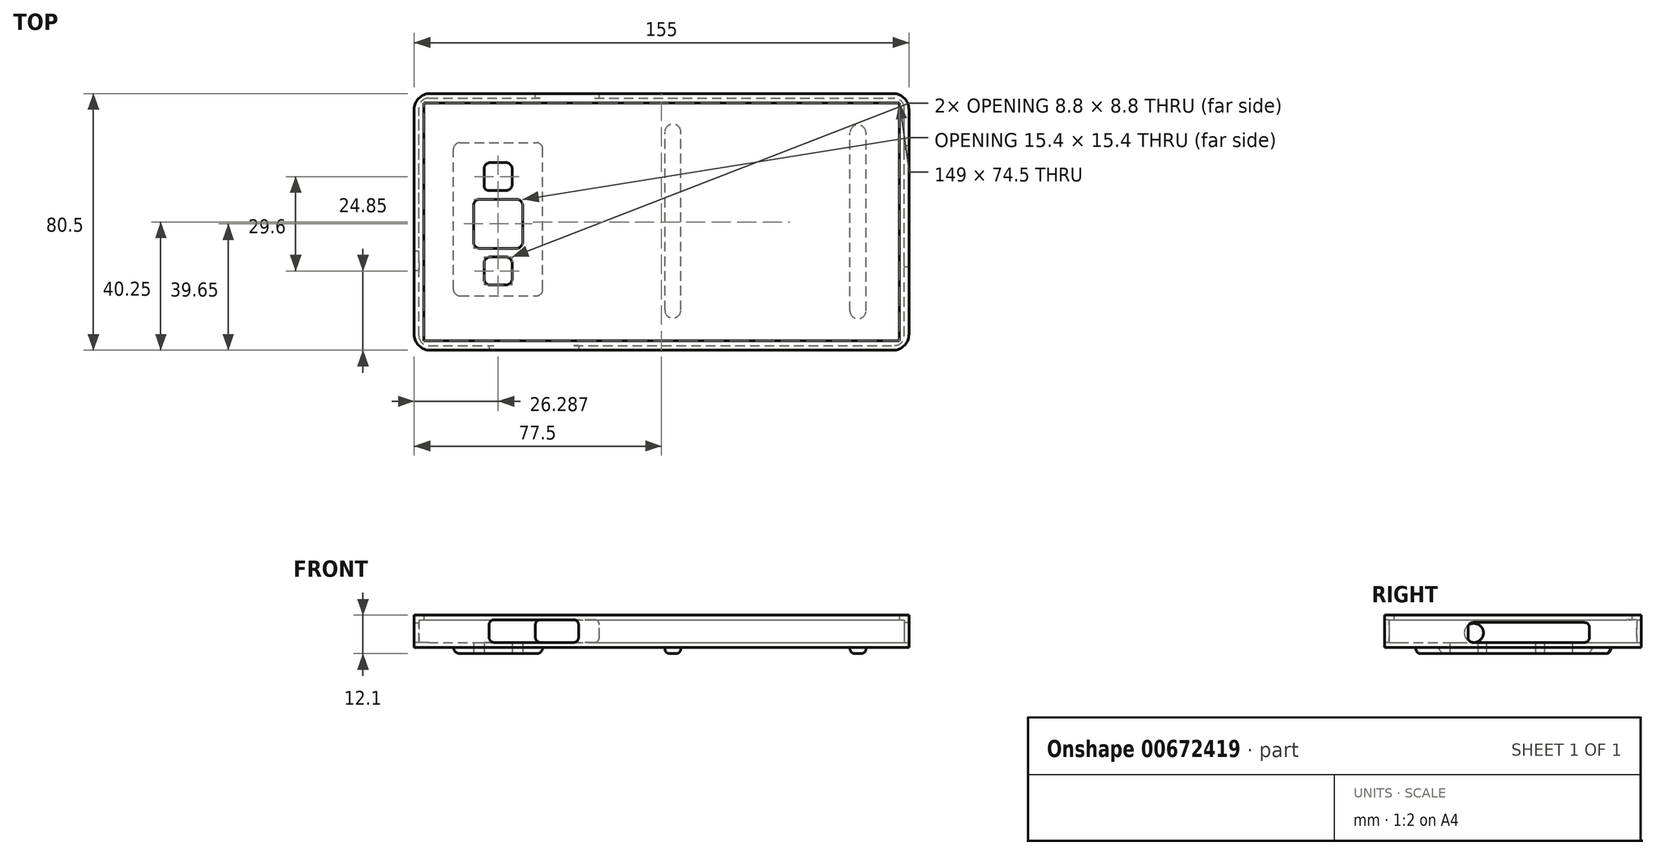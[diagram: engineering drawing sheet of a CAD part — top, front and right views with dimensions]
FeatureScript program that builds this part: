
annotation { "Feature Type Name" : "Feature", "Feature Type Description" : "" }
export const myFeature = defineFeature(function(context is Context, id is Id, definition is map)
    precondition{}
    {
        {
            var Q0;
            Q0=qCreatedBy(makeId("Top.planeOp"),FACE);
            var sketch = newSketch(context, id + "F0", { "sketchPlane" : qUnion([Q0])});
            skLineSegment(sketch, "E0.bottom", {"start": v(0, 0) * mm, "end": v(155, 0) * mm});
            skLineSegment(sketch, "E0.top", {"start": v(0, 80.5) * mm, "end": v(155, 80.5) * mm});
            skLineSegment(sketch, "E0.left", {"start": v(0, 0) * mm, "end": v(0, 80.5) * mm});
            skLineSegment(sketch, "E0.right", {"start": v(155, 0) * mm, "end": v(155, 80.5) * mm});
            skSolve(sketch);
        }
        {
            var Q0;
            Q0=qSketchRegion(id+"F0",true);
            extrude(context, id + "F1", {"entities" : qUnion([Q0]), "depth" : 8.6 * mm, "offsetDistance" : 25 * mm});
        }
        {
            var Q0;
            Q0=makeQuery(id+"F1.opExtrude","CAP_FACE",FACE,{"disambiguationData":[OSD([sQuery(id+"F0.wireOp",EDGE,"E0.bottom"),sQuery(id+"F0.wireOp",EDGE,"E0.top"),sQuery(id+"F0.wireOp",EDGE,"E0.left"),sQuery(id+"F0.wireOp",EDGE,"E0.right")])],"isStart":false});
            shell(context, id + "F2", {"entities" : qUnion([Q0]), "thickness" : 1.5 * mm});
        }
        {
            var Q0;
            Q0=makeQuery(id+"F1.opExtrude","CAP_FACE",FACE,{"disambiguationData":[OSD([sQuery(id+"F0.wireOp",EDGE,"E0.bottom"),sQuery(id+"F0.wireOp",EDGE,"E0.top"),sQuery(id+"F0.wireOp",EDGE,"E0.left"),sQuery(id+"F0.wireOp",EDGE,"E0.right")])],"isStart":false});
            var sketch = newSketch(context, id + "F3", { "sketchPlane" : qUnion([Q0])});
            skLineSegment(sketch, "E1.0", {"start": v(3, 77.5) * mm, "end": v(152, 77.5) * mm});
            skLineSegment(sketch, "E1.1", {"start": v(3, 3) * mm, "end": v(3, 77.5) * mm});
            skLineSegment(sketch, "E1.2", {"start": v(3, 3) * mm, "end": v(152, 3) * mm});
            skLineSegment(sketch, "E1.3", {"start": v(152, 3) * mm, "end": v(152, 77.5) * mm});
            skSolve(sketch);
        }
        {
            var Q0;
            Q0=makeQuery(id+"F3.imprint","IMPRINT",FACE,{"disambiguationData":[TD([[makeQuery(id+"F3.imprint","IMPRINT",EDGE,{"derivedFrom":sQuery(id+"F3.wireOp",EDGE,"E1.0")}),1.0]])]});
            var Q1;
            {var subQ6=sQuery(id+"F0.wireOp",EDGE,"E0.bottom");var subQ7=makeQuery(id+"F1.opExtrude","CAP_EDGE",EDGE,{"disambiguationData":[OSD([subQ6])],"isStart":false});Q1=makeQuery(id+"F3.imprint","IMPRINT",FACE,{"disambiguationData":[TD([[makeQuery(id+"F3.imprint","IMPRINT",EDGE,{"derivedFrom":subQ7}),1.0]])]});}
            extrude(context, id + "F4", {"entities" : qUnion([Q0, Q1]), "operationType" : NewBodyOperationType.ADD, "depth" : 1.5 * mm, "offsetDistance" : 25 * mm});
        }
        {
            var Q0;
            {var subQ0=sQuery(id+"F0.wireOp",EDGE,"E0.bottom");Q0=makeQuery(id+"F4.boolean.opBoolean","MERGE",FACE,{"derivedFrom":[makeQuery(id+"F1.opExtrude","SWEPT_FACE",FACE,{"disambiguationData":[OSD([subQ0])]}),makeQuery(id+"F4.opExtrude","SWEPT_FACE",FACE,{"disambiguationData":[OSD([subQ0])]})]});}
            var sketch = newSketch(context, id + "F5", { "sketchPlane" : qUnion([Q0])});
            skLineSegment(sketch, "E2.bottom", {"start": v(23.5, 8.6) * mm, "end": v(51.5, 8.6) * mm});
            skLineSegment(sketch, "E2.top", {"start": v(23.5, 1.5) * mm, "end": v(51.5, 1.5) * mm});
            skLineSegment(sketch, "E2.left", {"start": v(23.5, 8.6) * mm, "end": v(23.5, 1.5) * mm});
            skLineSegment(sketch, "E2.right", {"start": v(51.5, 8.6) * mm, "end": v(51.5, 1.5) * mm});
            skSolve(sketch);
        }
        {
            var Q0;
            Q0=makeQuery(id+"F5.imprint","IMPRINT",FACE,{"disambiguationData":[TD([[makeQuery(id+"F5.imprint","IMPRINT",EDGE,{"derivedFrom":sQuery(id+"F5.wireOp",EDGE,"E2.bottom")}),-1.0]])]});
            extrude(context, id + "F6", {"entities" : qUnion([Q0]), "operationType" : NewBodyOperationType.REMOVE, "endBound" : BoundingType.UP_TO_NEXT, "oppositeDirection" : true, "depth" : 25 * mm, "offsetDistance" : 25 * mm});
        }
        {
            var Q0;
            {var subQ0=sQuery(id+"F0.wireOp",EDGE,"E0.top");Q0=makeQuery(id+"F4.boolean.opBoolean","MERGE",FACE,{"derivedFrom":[makeQuery(id+"F1.opExtrude","SWEPT_FACE",FACE,{"disambiguationData":[OSD([subQ0])]}),makeQuery(id+"F4.opExtrude","SWEPT_FACE",FACE,{"disambiguationData":[OSD([subQ0])]})]});}
            var sketch = newSketch(context, id + "F7", { "sketchPlane" : qUnion([Q0])});
            skLineSegment(sketch, "E3.bottom", {"start": v(-58, 8.6) * mm, "end": v(-38, 8.6) * mm});
            skLineSegment(sketch, "E3.top", {"start": v(-58, 1.5) * mm, "end": v(-38, 1.5) * mm});
            skLineSegment(sketch, "E3.left", {"start": v(-58, 8.6) * mm, "end": v(-58, 1.5) * mm});
            skLineSegment(sketch, "E3.right", {"start": v(-38, 8.6) * mm, "end": v(-38, 1.5) * mm});
            skSolve(sketch);
        }
        {
            var Q0;
            Q0=makeQuery(id+"F7.imprint","IMPRINT",FACE,{"disambiguationData":[TD([[makeQuery(id+"F7.imprint","IMPRINT",EDGE,{"derivedFrom":sQuery(id+"F7.wireOp",EDGE,"E3.bottom")}),-1.0]])]});
            extrude(context, id + "F8", {"entities" : qUnion([Q0]), "operationType" : NewBodyOperationType.REMOVE, "endBound" : BoundingType.UP_TO_NEXT, "oppositeDirection" : true, "depth" : 25 * mm, "offsetDistance" : 25 * mm});
        }
        {
            var Q0;
            {var subQ0=sQuery(id+"F0.wireOp",EDGE,"E0.left");Q0=makeQuery(id+"F4.boolean.opBoolean","MERGE",FACE,{"derivedFrom":[makeQuery(id+"F1.opExtrude","SWEPT_FACE",FACE,{"disambiguationData":[OSD([subQ0])]}),makeQuery(id+"F4.opExtrude","SWEPT_FACE",FACE,{"disambiguationData":[OSD([subQ0])]})]});}
            var sketch = newSketch(context, id + "F9", { "sketchPlane" : qUnion([Q0])});
            skCircle(sketch, "E4", {"center": v(-28, 4.5) * mm, "radius": 3 * mm});
            skSolve(sketch);
        }
        {
            var Q0;
            Q0=makeQuery(id+"F9.imprint","IMPRINT",FACE,{"disambiguationData":[TD([[makeQuery(id+"F9.imprint","IMPRINT",EDGE,{"derivedFrom":sQuery(id+"F9.wireOp",EDGE,"E4")}),1.0]])]});
            extrude(context, id + "F10", {"entities" : qUnion([Q0]), "operationType" : NewBodyOperationType.REMOVE, "endBound" : BoundingType.UP_TO_NEXT, "oppositeDirection" : true, "depth" : 25 * mm, "offsetDistance" : 25 * mm});
        }
        {
            var Q0;
            {var subQ0=sQuery(id+"F0.wireOp",EDGE,"E0.right");Q0=makeQuery(id+"F4.boolean.opBoolean","MERGE",FACE,{"derivedFrom":[makeQuery(id+"F1.opExtrude","SWEPT_FACE",FACE,{"disambiguationData":[OSD([subQ0])]}),makeQuery(id+"F4.opExtrude","SWEPT_FACE",FACE,{"disambiguationData":[OSD([subQ0])]})]});}
            var sketch = newSketch(context, id + "F11", { "sketchPlane" : qUnion([Q0])});
            skLineSegment(sketch, "E5.bottom", {"start": v(26.2, 7.75) * mm, "end": v(64.2, 7.75) * mm});
            skLineSegment(sketch, "E5.top", {"start": v(26.2, 1.5) * mm, "end": v(64.2, 1.5) * mm});
            skLineSegment(sketch, "E5.left", {"start": v(26.2, 7.75) * mm, "end": v(26.2, 1.5) * mm});
            skLineSegment(sketch, "E5.right", {"start": v(64.2, 7.75) * mm, "end": v(64.2, 1.5) * mm});
            skSolve(sketch);
        }
        {
            var Q0;
            Q0=makeQuery(id+"F11.imprint","IMPRINT",FACE,{"disambiguationData":[TD([[makeQuery(id+"F11.imprint","IMPRINT",EDGE,{"derivedFrom":sQuery(id+"F11.wireOp",EDGE,"E5.bottom")}),-1.0]])]});
            extrude(context, id + "F12", {"entities" : qUnion([Q0]), "operationType" : NewBodyOperationType.REMOVE, "endBound" : BoundingType.UP_TO_NEXT, "oppositeDirection" : true, "depth" : 25 * mm, "offsetDistance" : 25 * mm});
        }
        {
            var Q0;
            Q0=makeQuery(id+"F1.opExtrude","CAP_FACE",FACE,{"disambiguationData":[OSD([sQuery(id+"F0.wireOp",EDGE,"E0.bottom"),sQuery(id+"F0.wireOp",EDGE,"E0.top"),sQuery(id+"F0.wireOp",EDGE,"E0.left"),sQuery(id+"F0.wireOp",EDGE,"E0.right")])],"isStart":true});
            var sketch = newSketch(context, id + "F13", { "sketchPlane" : qUnion([Q0])});
            skLineSegment(sketch, "E6.bottom", {"start": v(21.89, -20.45) * mm, "end": v(30.69, -20.45) * mm});
            skLineSegment(sketch, "E6.top", {"start": v(21.89, -29.25) * mm, "end": v(30.69, -29.25) * mm});
            skLineSegment(sketch, "E6.left", {"start": v(21.89, -20.45) * mm, "end": v(21.89, -29.25) * mm});
            skLineSegment(sketch, "E6.right", {"start": v(30.69, -20.45) * mm, "end": v(30.69, -29.25) * mm});
            skLineSegment(sketch, "E7.bottom", {"start": v(18.59, -31.95) * mm, "end": v(33.99, -31.95) * mm});
            skLineSegment(sketch, "E7.top", {"start": v(18.59, -47.35) * mm, "end": v(33.99, -47.35) * mm});
            skLineSegment(sketch, "E7.left", {"start": v(18.59, -31.95) * mm, "end": v(18.59, -47.35) * mm});
            skLineSegment(sketch, "E7.right", {"start": v(33.99, -31.95) * mm, "end": v(33.99, -47.35) * mm});
            skLineSegment(sketch, "E8.bottom", {"start": v(21.89, -50.05) * mm, "end": v(30.69, -50.05) * mm});
            skLineSegment(sketch, "E8.top", {"start": v(21.89, -58.85) * mm, "end": v(30.69, -58.85) * mm});
            skLineSegment(sketch, "E8.left", {"start": v(21.89, -50.05) * mm, "end": v(21.89, -58.85) * mm});
            skLineSegment(sketch, "E8.right", {"start": v(30.69, -50.05) * mm, "end": v(30.69, -58.85) * mm});
            skLineSegment(sketch, "E9", {"start": v(12.52, -39.65) * mm, "end": v(41, -39.65) * mm});
            skPoint(sketch, "E9.startSnap0", {"position": v(18.59, -39.65) * mm});
            skLineSegment(sketch, "E10", {"start": v(16.62, -24.85) * mm, "end": v(34.64, -24.85) * mm});
            skPoint(sketch, "E10.startSnap0", {"position": v(21.89, -24.85) * mm});
            skLineSegment(sketch, "E11", {"start": v(16.41, -54.45) * mm, "end": v(34.85, -54.45) * mm});
            skPoint(sketch, "E11.startSnap0", {"position": v(21.89, -54.45) * mm});
            skSolve(sketch);
        }
        {
            var Q0;
            {var subQ0=sQuery(id+"F13.wireOp",EDGE,"E6.top");Q0=makeQuery(id+"F13.imprint","IMPRINT",FACE,{"disambiguationData":[TD([[makeQuery(id+"F13.imprint","IMPRINT",EDGE,{"derivedFrom":subQ0}),1.0]])]});}
            var Q1;
            {var subQ0=sQuery(id+"F13.wireOp",EDGE,"E6.bottom");Q1=makeQuery(id+"F13.imprint","IMPRINT",FACE,{"disambiguationData":[TD([[makeQuery(id+"F13.imprint","IMPRINT",EDGE,{"derivedFrom":subQ0}),-1.0]])]});}
            var Q2;
            {var subQ0=sQuery(id+"F13.wireOp",EDGE,"E7.bottom");Q2=makeQuery(id+"F13.imprint","IMPRINT",FACE,{"disambiguationData":[TD([[makeQuery(id+"F13.imprint","IMPRINT",EDGE,{"derivedFrom":subQ0}),-1.0]])]});}
            var Q3;
            {var subQ0=sQuery(id+"F13.wireOp",EDGE,"E7.top");Q3=makeQuery(id+"F13.imprint","IMPRINT",FACE,{"disambiguationData":[TD([[makeQuery(id+"F13.imprint","IMPRINT",EDGE,{"derivedFrom":subQ0}),1.0]])]});}
            var Q4;
            {var subQ0=sQuery(id+"F13.wireOp",EDGE,"E8.bottom");Q4=makeQuery(id+"F13.imprint","IMPRINT",FACE,{"disambiguationData":[TD([[makeQuery(id+"F13.imprint","IMPRINT",EDGE,{"derivedFrom":subQ0}),-1.0]])]});}
            var Q5;
            {var subQ0=sQuery(id+"F13.wireOp",EDGE,"E8.top");Q5=makeQuery(id+"F13.imprint","IMPRINT",FACE,{"disambiguationData":[TD([[makeQuery(id+"F13.imprint","IMPRINT",EDGE,{"derivedFrom":subQ0}),1.0]])]});}
            extrude(context, id + "F14", {"entities" : qUnion([Q0, Q1, Q2, Q3, Q4, Q5]), "operationType" : NewBodyOperationType.REMOVE, "endBound" : BoundingType.UP_TO_NEXT, "oppositeDirection" : true, "depth" : 25 * mm, "offsetDistance" : 25 * mm});
        }
        {
            var Q0;
            Q0=makeQuery(id+"F6.boolean.opBoolean","COPY",EDGE,{"derivedFrom":makeQuery(id+"F6.opExtrude","SWEPT_EDGE",EDGE,{"disambiguationData":[OSD([sQuery(id+"F5.wireOp",EDGE,"E2.bottom"),sQuery(id+"F5.wireOp",EDGE,"E2.left")])]})});
            var Q1;
            Q1=makeQuery(id+"F6.boolean.opBoolean","COPY",EDGE,{"derivedFrom":makeQuery(id+"F6.opExtrude","SWEPT_EDGE",EDGE,{"disambiguationData":[OSD([sQuery(id+"F5.wireOp",EDGE,"E2.bottom"),sQuery(id+"F5.wireOp",EDGE,"E2.right")])]})});
            var Q2;
            Q2=makeQuery(id+"F6.boolean.opBoolean","COPY",EDGE,{"derivedFrom":makeQuery(id+"F6.opExtrude","SWEPT_EDGE",EDGE,{"disambiguationData":[OSD([sQuery(id+"F5.wireOp",EDGE,"E2.top"),sQuery(id+"F5.wireOp",EDGE,"E2.right")])]})});
            var Q3;
            Q3=makeQuery(id+"F6.boolean.opBoolean","COPY",EDGE,{"derivedFrom":makeQuery(id+"F6.opExtrude","SWEPT_EDGE",EDGE,{"disambiguationData":[OSD([sQuery(id+"F5.wireOp",EDGE,"E2.top"),sQuery(id+"F5.wireOp",EDGE,"E2.left")])]})});
            var Q4;
            Q4=makeQuery(id+"F12.boolean.opBoolean","COPY",EDGE,{"derivedFrom":makeQuery(id+"F12.opExtrude","SWEPT_EDGE",EDGE,{"disambiguationData":[OSD([sQuery(id+"F11.wireOp",EDGE,"E5.bottom"),sQuery(id+"F11.wireOp",EDGE,"E5.left")])]})});
            var Q5;
            Q5=makeQuery(id+"F12.boolean.opBoolean","COPY",EDGE,{"derivedFrom":makeQuery(id+"F12.opExtrude","SWEPT_EDGE",EDGE,{"disambiguationData":[OSD([sQuery(id+"F11.wireOp",EDGE,"E5.top"),sQuery(id+"F11.wireOp",EDGE,"E5.left")])]})});
            var Q6;
            Q6=makeQuery(id+"F12.boolean.opBoolean","COPY",EDGE,{"derivedFrom":makeQuery(id+"F12.opExtrude","SWEPT_EDGE",EDGE,{"disambiguationData":[OSD([sQuery(id+"F11.wireOp",EDGE,"E5.bottom"),sQuery(id+"F11.wireOp",EDGE,"E5.right")])]})});
            var Q7;
            Q7=makeQuery(id+"F12.boolean.opBoolean","COPY",EDGE,{"derivedFrom":makeQuery(id+"F12.opExtrude","SWEPT_EDGE",EDGE,{"disambiguationData":[OSD([sQuery(id+"F11.wireOp",EDGE,"E5.top"),sQuery(id+"F11.wireOp",EDGE,"E5.right")])]})});
            var Q8;
            Q8=makeQuery(id+"F8.boolean.opBoolean","COPY",EDGE,{"derivedFrom":makeQuery(id+"F8.opExtrude","SWEPT_EDGE",EDGE,{"disambiguationData":[OSD([sQuery(id+"F7.wireOp",EDGE,"E3.bottom"),sQuery(id+"F7.wireOp",EDGE,"E3.left")])]})});
            var Q9;
            Q9=makeQuery(id+"F8.boolean.opBoolean","COPY",EDGE,{"derivedFrom":makeQuery(id+"F8.opExtrude","SWEPT_EDGE",EDGE,{"disambiguationData":[OSD([sQuery(id+"F7.wireOp",EDGE,"E3.top"),sQuery(id+"F7.wireOp",EDGE,"E3.left")])]})});
            var Q10;
            Q10=makeQuery(id+"F8.boolean.opBoolean","COPY",EDGE,{"derivedFrom":makeQuery(id+"F8.opExtrude","SWEPT_EDGE",EDGE,{"disambiguationData":[OSD([sQuery(id+"F7.wireOp",EDGE,"E3.bottom"),sQuery(id+"F7.wireOp",EDGE,"E3.right")])]})});
            var Q11;
            Q11=makeQuery(id+"F8.boolean.opBoolean","COPY",EDGE,{"derivedFrom":makeQuery(id+"F8.opExtrude","SWEPT_EDGE",EDGE,{"disambiguationData":[OSD([sQuery(id+"F7.wireOp",EDGE,"E3.top"),sQuery(id+"F7.wireOp",EDGE,"E3.right")])]})});
            var Q12;
            Q12=makeQuery(id+"F14.boolean.opBoolean","COPY",EDGE,{"derivedFrom":makeQuery(id+"F14.opExtrude","SWEPT_EDGE",EDGE,{"disambiguationData":[OSD([sQuery(id+"F13.wireOp",EDGE,"E8.bottom"),sQuery(id+"F13.wireOp",EDGE,"E8.left")])]})});
            fillet(context, id + "F15", {"entities" : qUnion([Q0, Q1, Q2, Q3, Q4, Q5, Q6, Q7, Q8, Q9, Q10, Q11, Q12]), "radius" : 1.5 * mm, "tangentPropagation" : true, "allowEdgeOverflow" : false});
        }
        {
            var Q0;
            Q0=makeQuery(id+"F14.boolean.opBoolean","COPY",EDGE,{"derivedFrom":makeQuery(id+"F14.opExtrude","SWEPT_EDGE",EDGE,{"disambiguationData":[OSD([sQuery(id+"F13.wireOp",EDGE,"E6.top"),sQuery(id+"F13.wireOp",EDGE,"E6.left")])]})});
            var Q1;
            Q1=makeQuery(id+"F14.boolean.opBoolean","COPY",EDGE,{"derivedFrom":makeQuery(id+"F14.opExtrude","SWEPT_EDGE",EDGE,{"disambiguationData":[OSD([sQuery(id+"F13.wireOp",EDGE,"E7.top"),sQuery(id+"F13.wireOp",EDGE,"E7.left")])]})});
            var Q2;
            Q2=makeQuery(id+"F14.boolean.opBoolean","COPY",EDGE,{"derivedFrom":makeQuery(id+"F14.opExtrude","SWEPT_EDGE",EDGE,{"disambiguationData":[OSD([sQuery(id+"F13.wireOp",EDGE,"E8.top"),sQuery(id+"F13.wireOp",EDGE,"E8.left")])]})});
            var Q3;
            Q3=makeQuery(id+"F14.boolean.opBoolean","COPY",EDGE,{"derivedFrom":makeQuery(id+"F14.opExtrude","SWEPT_EDGE",EDGE,{"disambiguationData":[OSD([sQuery(id+"F13.wireOp",EDGE,"E6.bottom"),sQuery(id+"F13.wireOp",EDGE,"E6.left")])]})});
            var Q4;
            Q4=makeQuery(id+"F14.boolean.opBoolean","COPY",EDGE,{"derivedFrom":makeQuery(id+"F14.opExtrude","SWEPT_EDGE",EDGE,{"disambiguationData":[OSD([sQuery(id+"F13.wireOp",EDGE,"E7.bottom"),sQuery(id+"F13.wireOp",EDGE,"E7.left")])]})});
            var Q5;
            Q5=makeQuery(id+"F14.boolean.opBoolean","COPY",EDGE,{"derivedFrom":makeQuery(id+"F14.opExtrude","SWEPT_EDGE",EDGE,{"disambiguationData":[OSD([sQuery(id+"F13.wireOp",EDGE,"E8.bottom"),sQuery(id+"F13.wireOp",EDGE,"E8.right")])]})});
            var Q6;
            Q6=makeQuery(id+"F14.boolean.opBoolean","COPY",EDGE,{"derivedFrom":makeQuery(id+"F14.opExtrude","SWEPT_EDGE",EDGE,{"disambiguationData":[OSD([sQuery(id+"F13.wireOp",EDGE,"E7.bottom"),sQuery(id+"F13.wireOp",EDGE,"E7.right")])]})});
            var Q7;
            Q7=makeQuery(id+"F14.boolean.opBoolean","COPY",EDGE,{"derivedFrom":makeQuery(id+"F14.opExtrude","SWEPT_EDGE",EDGE,{"disambiguationData":[OSD([sQuery(id+"F13.wireOp",EDGE,"E6.bottom"),sQuery(id+"F13.wireOp",EDGE,"E6.right")])]})});
            var Q8;
            Q8=makeQuery(id+"F14.boolean.opBoolean","COPY",EDGE,{"derivedFrom":makeQuery(id+"F14.opExtrude","SWEPT_EDGE",EDGE,{"disambiguationData":[OSD([sQuery(id+"F13.wireOp",EDGE,"E6.top"),sQuery(id+"F13.wireOp",EDGE,"E6.right")])]})});
            var Q9;
            Q9=makeQuery(id+"F14.boolean.opBoolean","COPY",EDGE,{"derivedFrom":makeQuery(id+"F14.opExtrude","SWEPT_EDGE",EDGE,{"disambiguationData":[OSD([sQuery(id+"F13.wireOp",EDGE,"E7.top"),sQuery(id+"F13.wireOp",EDGE,"E7.right")])]})});
            var Q10;
            Q10=makeQuery(id+"F14.boolean.opBoolean","COPY",EDGE,{"derivedFrom":makeQuery(id+"F14.opExtrude","SWEPT_EDGE",EDGE,{"disambiguationData":[OSD([sQuery(id+"F13.wireOp",EDGE,"E8.top"),sQuery(id+"F13.wireOp",EDGE,"E8.right")])]})});
            fillet(context, id + "F16", {"entities" : qUnion([Q0, Q1, Q2, Q3, Q4, Q5, Q6, Q7, Q8, Q9, Q10]), "radius" : 2 * mm, "tangentPropagation" : true, "allowEdgeOverflow" : false});
        }
        {
            var Q0;
            {var subQ0=sQuery(id+"F0.wireOp",EDGE,"E0.left");var subQ1=sQuery(id+"F0.wireOp",EDGE,"E0.bottom");Q0=makeQuery(id+"F4.boolean.opBoolean","MERGE",EDGE,{"derivedFrom":[makeQuery(id+"F1.opExtrude","SWEPT_EDGE",EDGE,{"disambiguationData":[OSD([subQ1,subQ0])]}),makeQuery(id+"F4.opExtrude","SWEPT_EDGE",EDGE,{"disambiguationData":[OSD([subQ1,subQ0])]})]});}
            var Q1;
            {var subQ0=sQuery(id+"F0.wireOp",EDGE,"E0.left");var subQ1=sQuery(id+"F0.wireOp",EDGE,"E0.top");Q1=makeQuery(id+"F4.boolean.opBoolean","MERGE",EDGE,{"derivedFrom":[makeQuery(id+"F1.opExtrude","SWEPT_EDGE",EDGE,{"disambiguationData":[OSD([subQ1,subQ0])]}),makeQuery(id+"F4.opExtrude","SWEPT_EDGE",EDGE,{"disambiguationData":[OSD([subQ1,subQ0])]})]});}
            var Q2;
            {var subQ0=sQuery(id+"F0.wireOp",EDGE,"E0.right");var subQ1=sQuery(id+"F0.wireOp",EDGE,"E0.bottom");Q2=makeQuery(id+"F4.boolean.opBoolean","MERGE",EDGE,{"derivedFrom":[makeQuery(id+"F1.opExtrude","SWEPT_EDGE",EDGE,{"disambiguationData":[OSD([subQ1,subQ0])]}),makeQuery(id+"F4.opExtrude","SWEPT_EDGE",EDGE,{"disambiguationData":[OSD([subQ1,subQ0])]})]});}
            var Q3;
            {var subQ0=sQuery(id+"F0.wireOp",EDGE,"E0.right");var subQ1=sQuery(id+"F0.wireOp",EDGE,"E0.top");Q3=makeQuery(id+"F4.boolean.opBoolean","MERGE",EDGE,{"derivedFrom":[makeQuery(id+"F1.opExtrude","SWEPT_EDGE",EDGE,{"disambiguationData":[OSD([subQ1,subQ0])]}),makeQuery(id+"F4.opExtrude","SWEPT_EDGE",EDGE,{"disambiguationData":[OSD([subQ1,subQ0])]})]});}
            fillet(context, id + "F17", {"entities" : qUnion([Q0, Q1, Q2, Q3]), "radius" : 5 * mm, "tangentPropagation" : true, "allowEdgeOverflow" : false});
        }
        {
            var Q0;
            Q0=makeQuery(id+"F2.opShell","OFFSET_EDGE",EDGE,{"disambiguationData":[OSD([sQuery(id+"F0.wireOp",EDGE,"E0.top"),sQuery(id+"F0.wireOp",EDGE,"E0.left")])]});
            var Q1;
            Q1=makeQuery(id+"F2.opShell","OFFSET_EDGE",EDGE,{"disambiguationData":[OSD([sQuery(id+"F0.wireOp",EDGE,"E0.bottom"),sQuery(id+"F0.wireOp",EDGE,"E0.left")])]});
            var Q2;
            Q2=makeQuery(id+"F2.opShell","OFFSET_EDGE",EDGE,{"disambiguationData":[OSD([sQuery(id+"F0.wireOp",EDGE,"E0.top"),sQuery(id+"F0.wireOp",EDGE,"E0.right")])]});
            var Q3;
            Q3=makeQuery(id+"F2.opShell","OFFSET_EDGE",EDGE,{"disambiguationData":[OSD([sQuery(id+"F0.wireOp",EDGE,"E0.bottom"),sQuery(id+"F0.wireOp",EDGE,"E0.right")])]});
            fillet(context, id + "F18", {"entities" : qUnion([Q0, Q1, Q2, Q3]), "radius" : 3 * mm, "tangentPropagation" : true, "allowEdgeOverflow" : false});
        }
        {
            var Q0;
            Q0=makeQuery(id+"F1.opExtrude","CAP_FACE",FACE,{"disambiguationData":[OSD([sQuery(id+"F0.wireOp",EDGE,"E0.bottom"),sQuery(id+"F0.wireOp",EDGE,"E0.top"),sQuery(id+"F0.wireOp",EDGE,"E0.left"),sQuery(id+"F0.wireOp",EDGE,"E0.right")])],"isStart":true});
            var sketch = newSketch(context, id + "F19", { "sketchPlane" : qUnion([Q0])});
            skLineSegment(sketch, "E12.bottom", {"start": v(12.29, -17.07) * mm, "end": v(40.29, -17.07) * mm});
            skLineSegment(sketch, "E12.top", {"start": v(12.29, -65.07) * mm, "end": v(40.29, -65.07) * mm});
            skLineSegment(sketch, "E12.left", {"start": v(12.29, -17.07) * mm, "end": v(12.29, -65.07) * mm});
            skLineSegment(sketch, "E12.right", {"start": v(40.29, -17.07) * mm, "end": v(40.29, -65.07) * mm});
            skLineSegment(sketch, "E13", {"start": v(26.29, -8.1) * mm, "end": v(26.29, -68.89) * mm});
            skPoint(sketch, "E13.startSnap0", {"position": v(26.29, -20.45) * mm});
            skSolve(sketch);
        }
        {
            var Q0;
            {var subQ26=sQuery(id+"F19.wireOp",EDGE,"E12.left");Q0=makeQuery(id+"F19.imprint","IMPRINT",FACE,{"disambiguationData":[TD([[makeQuery(id+"F19.imprint","IMPRINT",EDGE,{"derivedFrom":subQ26}),1.0]])]});}
            var Q1;
            {var subQ25=sQuery(id+"F19.wireOp",EDGE,"E12.right");Q1=makeQuery(id+"F19.imprint","IMPRINT",FACE,{"disambiguationData":[TD([[makeQuery(id+"F19.imprint","IMPRINT",EDGE,{"derivedFrom":subQ25}),-1.0]])]});}
            extrude(context, id + "F20", {"entities" : qUnion([Q0, Q1]), "operationType" : NewBodyOperationType.ADD, "depth" : 2 * mm, "offsetDistance" : 25 * mm});
        }
        {
            var Q0;
            Q0=makeQuery(id+"F20.opExtrude","SWEPT_EDGE",EDGE,{"disambiguationData":[OSD([sQuery(id+"F19.wireOp",EDGE,"E12.bottom"),sQuery(id+"F19.wireOp",EDGE,"E12.left")])]});
            var Q1;
            Q1=makeQuery(id+"F20.opExtrude","SWEPT_EDGE",EDGE,{"disambiguationData":[OSD([sQuery(id+"F19.wireOp",EDGE,"E12.bottom"),sQuery(id+"F19.wireOp",EDGE,"E12.right")])]});
            var Q2;
            Q2=makeQuery(id+"F20.opExtrude","SWEPT_EDGE",EDGE,{"disambiguationData":[OSD([sQuery(id+"F19.wireOp",EDGE,"E12.top"),sQuery(id+"F19.wireOp",EDGE,"E12.left")])]});
            var Q3;
            Q3=makeQuery(id+"F20.opExtrude","SWEPT_EDGE",EDGE,{"disambiguationData":[OSD([sQuery(id+"F19.wireOp",EDGE,"E12.top"),sQuery(id+"F19.wireOp",EDGE,"E12.right")])]});
            var Q4;
            Q4=makeQuery(id+"F20.opExtrude","CAP_EDGE",EDGE,{"disambiguationData":[OSD([sQuery(id+"F19.wireOp",EDGE,"E12.left")])],"isStart":false});
            var Q5;
            Q5=makeQuery(id+"F20.opExtrude","CAP_EDGE",EDGE,{"disambiguationData":[OSD([sQuery(id+"F19.wireOp",EDGE,"E12.top")])],"isStart":false});
            var Q6;
            Q6=makeQuery(id+"F20.opExtrude","CAP_EDGE",EDGE,{"disambiguationData":[OSD([sQuery(id+"F19.wireOp",EDGE,"E12.right")])],"isStart":false});
            var Q7;
            Q7=makeQuery(id+"F20.opExtrude","CAP_EDGE",EDGE,{"disambiguationData":[OSD([sQuery(id+"F19.wireOp",EDGE,"E12.bottom")])],"isStart":false});
            fillet(context, id + "F21", {"entities" : qUnion([Q0, Q1, Q2, Q3, Q4, Q5, Q6, Q7]), "radius" : 2 * mm, "tangentPropagation" : true, "allowEdgeOverflow" : false});
        }
        {
            var Q0;
            Q0=makeQuery(id+"F1.opExtrude","CAP_FACE",FACE,{"disambiguationData":[OSD([sQuery(id+"F0.wireOp",EDGE,"E0.bottom"),sQuery(id+"F0.wireOp",EDGE,"E0.top"),sQuery(id+"F0.wireOp",EDGE,"E0.left"),sQuery(id+"F0.wireOp",EDGE,"E0.right")])],"isStart":true});
            var sketch = newSketch(context, id + "F22", { "sketchPlane" : qUnion([Q0])});
            skLineSegment(sketch, "E14.bottom", {"start": v(139.03, -9.85) * mm, "end": v(139.03, -9.85) * mm});
            skLineSegment(sketch, "E14.top", {"start": v(139.03, -70.65) * mm, "end": v(139.03, -70.65) * mm});
            skLineSegment(sketch, "E14.left", {"start": v(136.53, -12.35) * mm, "end": v(136.53, -68.15) * mm});
            skLineSegment(sketch, "E14.right", {"start": v(141.53, -12.35) * mm, "end": v(141.53, -68.15) * mm});
            skLineSegment(sketch, "E15", {"start": v(128.65, -40.25) * mm, "end": v(162.75, -40.25) * mm});
            skPoint(sketch, "E15.startSnap0", {"position": v(136.53, -40.25) * mm});
            skPoint(sketch, "E16.visualSharp", {"position": v(136.53, -9.85) * mm});
            skArc(sketch, "E16.filletArc", {"start": v(139.03, -9.85) * mm, "mid": v(137.27, -10.58) * mm, "end": v(136.53, -12.35) * mm});
            skPoint(sketch, "E17.visualSharp", {"position": v(141.53, -9.85) * mm});
            skArc(sketch, "E17.filletArc", {"start": v(141.53, -12.35) * mm, "mid": v(140.8, -10.58) * mm, "end": v(139.03, -9.85) * mm});
            skPoint(sketch, "E18.visualSharp", {"position": v(136.53, -70.65) * mm});
            skArc(sketch, "E18.filletArc", {"start": v(136.53, -68.15) * mm, "mid": v(137.27, -69.92) * mm, "end": v(139.03, -70.65) * mm});
            skPoint(sketch, "E19.visualSharp", {"position": v(141.53, -70.65) * mm});
            skArc(sketch, "E19.filletArc", {"start": v(139.03, -70.65) * mm, "mid": v(140.8, -69.92) * mm, "end": v(141.53, -68.15) * mm});
            skLineSegment(sketch, "E20.1.0.0", {"start": v(78.53, -12.6) * mm, "end": v(78.53, -68.4) * mm});
            skLineSegment(sketch, "E20.1.0.1", {"start": v(83.53, -12.6) * mm, "end": v(83.53, -68.4) * mm});
            skArc(sketch, "E20.1.0.2", {"start": v(81.03, -10.1) * mm, "mid": v(79.27, -10.83) * mm, "end": v(78.53, -12.6) * mm});
            skArc(sketch, "E20.1.0.3", {"start": v(83.53, -12.6) * mm, "mid": v(82.8, -10.83) * mm, "end": v(81.03, -10.1) * mm});
            skArc(sketch, "E20.1.0.4", {"start": v(78.53, -68.4) * mm, "mid": v(79.27, -70.17) * mm, "end": v(81.03, -70.9) * mm});
            skArc(sketch, "E20.1.0.5", {"start": v(81.03, -70.9) * mm, "mid": v(82.8, -70.17) * mm, "end": v(83.53, -68.4) * mm});
            skLineSegment(sketch, "E20.direction1", {"start": v(136.53, -68.15) * mm, "end": v(78.53, -68.4) * mm, "construction": true});
            skSolve(sketch);
        }
        {
            var Q0;
            {var subQ6=sQuery(id+"F22.wireOp",EDGE,"E16.filletArc");Q0=makeQuery(id+"F22.imprint","IMPRINT",FACE,{"disambiguationData":[TD([[makeQuery(id+"F22.imprint","IMPRINT",EDGE,{"derivedFrom":subQ6}),1.0]])]});}
            var Q1;
            {var subQ0=sQuery(id+"F22.wireOp",EDGE,"E18.filletArc");Q1=makeQuery(id+"F22.imprint","IMPRINT",FACE,{"disambiguationData":[TD([[makeQuery(id+"F22.imprint","IMPRINT",EDGE,{"derivedFrom":subQ0}),1.0]])]});}
            extrude(context, id + "F23", {"entities" : qUnion([Q0, Q1]), "operationType" : NewBodyOperationType.ADD, "depth" : 2 * mm, "offsetDistance" : 25 * mm});
        }
        {
            var Q0;
            Q0=makeQuery(id+"F23.opExtrude","CAP_EDGE",EDGE,{"disambiguationData":[OSD([sQuery(id+"F22.wireOp",EDGE,"E16.filletArc"),sQuery(id+"F22.wireOp",EDGE,"E17.filletArc")])],"isStart":false});
            fillet(context, id + "F24", {"entities" : qUnion([Q0]), "radius" : 1.5 * mm, "tangentPropagation" : true, "allowEdgeOverflow" : false});
        }
        {
            var Q0;
            Q0=makeQuery(id+"F22.imprint","IMPRINT",FACE,{"disambiguationData":[TD([[makeQuery(id+"F22.imprint","IMPRINT",EDGE,{"derivedFrom":sQuery(id+"F22.wireOp",EDGE,"E20.1.0.0")}),1.0]])]});
            extrude(context, id + "F25", {"entities" : qUnion([Q0]), "operationType" : NewBodyOperationType.ADD, "depth" : 2 * mm, "offsetDistance" : 25 * mm});
        }
        {
            var Q0;
            Q0=makeQuery(id+"F25.opExtrude","CAP_EDGE",EDGE,{"disambiguationData":[OSD([sQuery(id+"F22.wireOp",EDGE,"E20.1.0.0")])],"isStart":false});
            fillet(context, id + "F26", {"entities" : qUnion([Q0]), "radius" : 1.5 * mm, "tangentPropagation" : true, "allowEdgeOverflow" : false});
        }
    });
